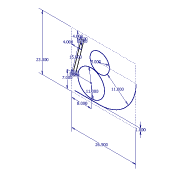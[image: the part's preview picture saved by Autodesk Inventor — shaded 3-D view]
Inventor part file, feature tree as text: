
AUTODESK INVENTOR PART (.ipt)
format: ipt  version: 2012 (Build 160160000, 160)  size: 77,312 bytes
history: native  units: in
note: dims shown in document units (in); Inventor stores cm internally (conversion verified against a paired STEP export)
features: sketch x1
ambient origin geometry x8: Origin, YZ Plane, XZ Plane, XY Plane, X Axis, Y Axis, Z Axis, Center Point
feature tree (1):
  sketch  "Sketch1"  dims[d0=23.0in d1=26.5in d2=8.0in d4=11.0in d5=1.0in d7=11.0in d9=1.0in d10=0.5in d11=0.5in d12=15.0in d13=2.0in d14=4.0in d15=4.0in d16=0.5in d17=8.0in d18=7.0in]
